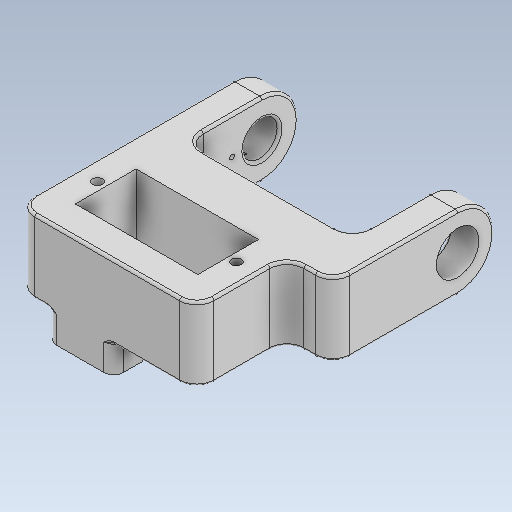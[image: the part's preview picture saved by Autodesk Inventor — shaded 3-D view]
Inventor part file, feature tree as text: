
AUTODESK INVENTOR PART (.ipt)
format: ipt  version: 2020.3 (Build 243373000, 373)  size: 346,624 bytes
history: native  units: mm
features: sketch x5, other x3
ambient origin geometry x8: Origin, YZ Plane, XZ Plane, XY Plane, X Axis, Y Axis, Z Axis, Center Point
bodies: Solid1 (feature_tree)
feature tree (8):
  other  "LegStart_v1.ipt"
  other  "Solid1::LegStart_v1.ipt"
  other  "TaggingFeature1"
  sketch  "Sketch1"  dims[d0=10.0mm]
  sketch  "Sketch2"
  sketch  "Sketch3"
  sketch  "Sketch8"
  sketch  "Sketch9"
